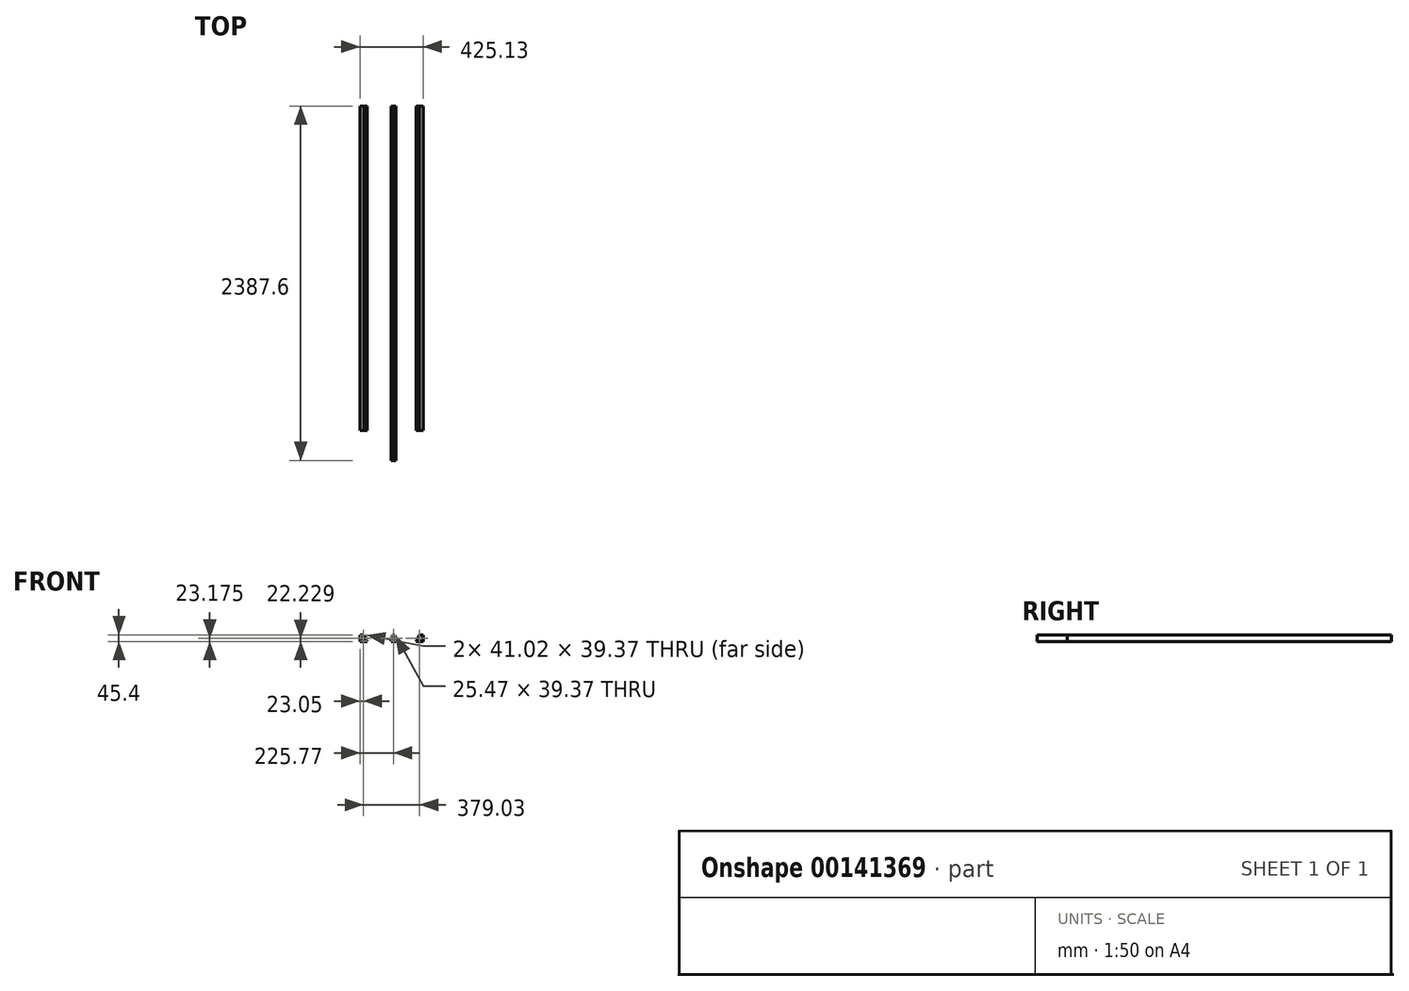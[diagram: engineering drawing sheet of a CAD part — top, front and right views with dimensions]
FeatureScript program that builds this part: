
annotation { "Feature Type Name" : "Feature", "Feature Type Description" : "" }
export const myFeature = defineFeature(function(context is Context, id is Id, definition is map)
    precondition{}
    {
        {
            var Q0;
            Q0=qCreatedBy(makeId("Front.planeOp"),FACE);
            var sketch = newSketch(context, id + "F0", { "sketchPlane" : qUnion([Q0])});
            skLineSegment(sketch, "E0.left", {"start": v(-203.31, 24.13) * mm, "end": v(-203.31, -20.32) * mm});
            skLineSegment(sketch, "E1", {"start": v(-203.31, 24.13) * mm, "end": v(-177.91, 24.13) * mm});
            skLineSegment(sketch, "E2", {"start": v(-177.91, 24.13) * mm, "end": v(-155.63, -20.32) * mm});
            skLineSegment(sketch, "E3", {"start": v(-155.63, -20.32) * mm, "end": v(-177.65, -20.32) * mm});
            skLineSegment(sketch, "E4", {"start": v(-177.65, -20.32) * mm, "end": v(-203.31, -20.32) * mm});
            skSolve(sketch);
        }
        {
            var Q0;
            Q0=makeQuery(id+"F0.imprint","IMPRINT",FACE,{"disambiguationData":[TD([[makeQuery(id+"F0.imprint","IMPRINT",EDGE,{"derivedFrom":sQuery(id+"F0.wireOp",EDGE,"E0.left")}),1.0]])]});
            extrude(context, id + "F1", {"entities" : qUnion([Q0]), "depth" : 2184.4 * mm});
        }
        {
            var Q0;
            Q0=makeQuery(id+"F1.opExtrude","CAP_FACE",FACE,{"disambiguationData":[OSD([sQuery(id+"F0.wireOp",EDGE,"E0.left"),sQuery(id+"F0.wireOp",EDGE,"E1"),sQuery(id+"F0.wireOp",EDGE,"E2"),sQuery(id+"F0.wireOp",EDGE,"E3"),sQuery(id+"F0.wireOp",EDGE,"E4")])],"isStart":false});
            var Q1;
            Q1=makeQuery(id+"F1.opExtrude","CAP_FACE",FACE,{"disambiguationData":[OSD([sQuery(id+"F0.wireOp",EDGE,"E0.left"),sQuery(id+"F0.wireOp",EDGE,"E1"),sQuery(id+"F0.wireOp",EDGE,"E2"),sQuery(id+"F0.wireOp",EDGE,"E3"),sQuery(id+"F0.wireOp",EDGE,"E4")])],"isStart":true});
            shell(context, id + "F2", {"entities" : qUnion([Q0, Q1]), "thickness" : 2.54 * mm});
        }
        {
            var Q0;
            Q0=qCreatedBy(makeId("Front.planeOp"),FACE);
            var sketch = newSketch(context, id + "F3", { "sketchPlane" : qUnion([Q0])});
            skLineSegment(sketch, "E5", {"start": v(6.58, -21.27) * mm, "end": v(16.1, 23.18) * mm});
            skLineSegment(sketch, "E6.MirrorCS", {"start": v(38.33, -21.27) * mm, "end": v(28.8, 23.18) * mm});
            skLineSegment(sketch, "E7", {"start": v(6.58, -21.27) * mm, "end": v(38.33, -21.27) * mm});
            skLineSegment(sketch, "E8", {"start": v(28.8, 23.18) * mm, "end": v(16.1, 23.18) * mm});
            skSolve(sketch);
        }
        {
            var Q0;
            Q0=qCreatedBy(makeId("Front.planeOp"),FACE);
            var sketch = newSketch(context, id + "F4", { "sketchPlane" : qUnion([Q0])});
            skLineSegment(sketch, "E9.MirrorCS", {"start": v(221.82, 24.1) * mm, "end": v(221.82, -20.35) * mm});
            skLineSegment(sketch, "E10.MirrorCS", {"start": v(196.42, 24.1) * mm, "end": v(174.15, -20.35) * mm});
            skLineSegment(sketch, "E11.MirrorCS", {"start": v(221.82, 24.1) * mm, "end": v(196.42, 24.1) * mm});
            skLineSegment(sketch, "E12.MirrorCS", {"start": v(221.82, -20.35) * mm, "end": v(174.15, -20.35) * mm});
            skSolve(sketch);
        }
        {
            var Q0;
            Q0=makeQuery(id+"F3.imprint","IMPRINT",FACE,{"disambiguationData":[TD([[makeQuery(id+"F3.imprint","IMPRINT",EDGE,{"derivedFrom":sQuery(id+"F3.wireOp",EDGE,"E5")}),-1.0]])]});
            extrude(context, id + "F5", {"entities" : qUnion([Q0]), "depth" : 2387.6 * mm});
        }
        {
            var Q0;
            Q0=makeQuery(id+"F5.opExtrude","CAP_FACE",FACE,{"disambiguationData":[OSD([sQuery(id+"F3.wireOp",EDGE,"E5"),sQuery(id+"F3.wireOp",EDGE,"E6.MirrorCS"),sQuery(id+"F3.wireOp",EDGE,"E7"),sQuery(id+"F3.wireOp",EDGE,"E8")])],"isStart":true});
            var Q1;
            Q1=makeQuery(id+"F5.opExtrude","CAP_FACE",FACE,{"disambiguationData":[OSD([sQuery(id+"F3.wireOp",EDGE,"E5"),sQuery(id+"F3.wireOp",EDGE,"E6.MirrorCS"),sQuery(id+"F3.wireOp",EDGE,"E7"),sQuery(id+"F3.wireOp",EDGE,"E8")])],"isStart":false});
            shell(context, id + "F6", {"entities" : qUnion([Q0, Q1]), "thickness" : 2.54 * mm});
        }
        {
            var Q0;
            Q0=makeQuery(id+"F4.imprint","IMPRINT",FACE,{"disambiguationData":[TD([[makeQuery(id+"F4.imprint","IMPRINT",EDGE,{"derivedFrom":sQuery(id+"F4.wireOp",EDGE,"E9.MirrorCS")}),-1.0]])]});
            extrude(context, id + "F7", {"entities" : qUnion([Q0]), "depth" : 2184.4 * mm});
        }
        {
            var Q0;
            Q0=makeQuery(id+"F7.opExtrude","CAP_FACE",FACE,{"disambiguationData":[OSD([sQuery(id+"F4.wireOp",EDGE,"E9.MirrorCS"),sQuery(id+"F4.wireOp",EDGE,"E10.MirrorCS"),sQuery(id+"F4.wireOp",EDGE,"E11.MirrorCS"),sQuery(id+"F4.wireOp",EDGE,"E12.MirrorCS")])],"isStart":false});
            var Q1;
            Q1=makeQuery(id+"F7.opExtrude","CAP_FACE",FACE,{"disambiguationData":[OSD([sQuery(id+"F4.wireOp",EDGE,"E9.MirrorCS"),sQuery(id+"F4.wireOp",EDGE,"E10.MirrorCS"),sQuery(id+"F4.wireOp",EDGE,"E11.MirrorCS"),sQuery(id+"F4.wireOp",EDGE,"E12.MirrorCS")])],"isStart":true});
            shell(context, id + "F8", {"entities" : qUnion([Q0, Q1]), "thickness" : 2.54 * mm});
        }
    });
